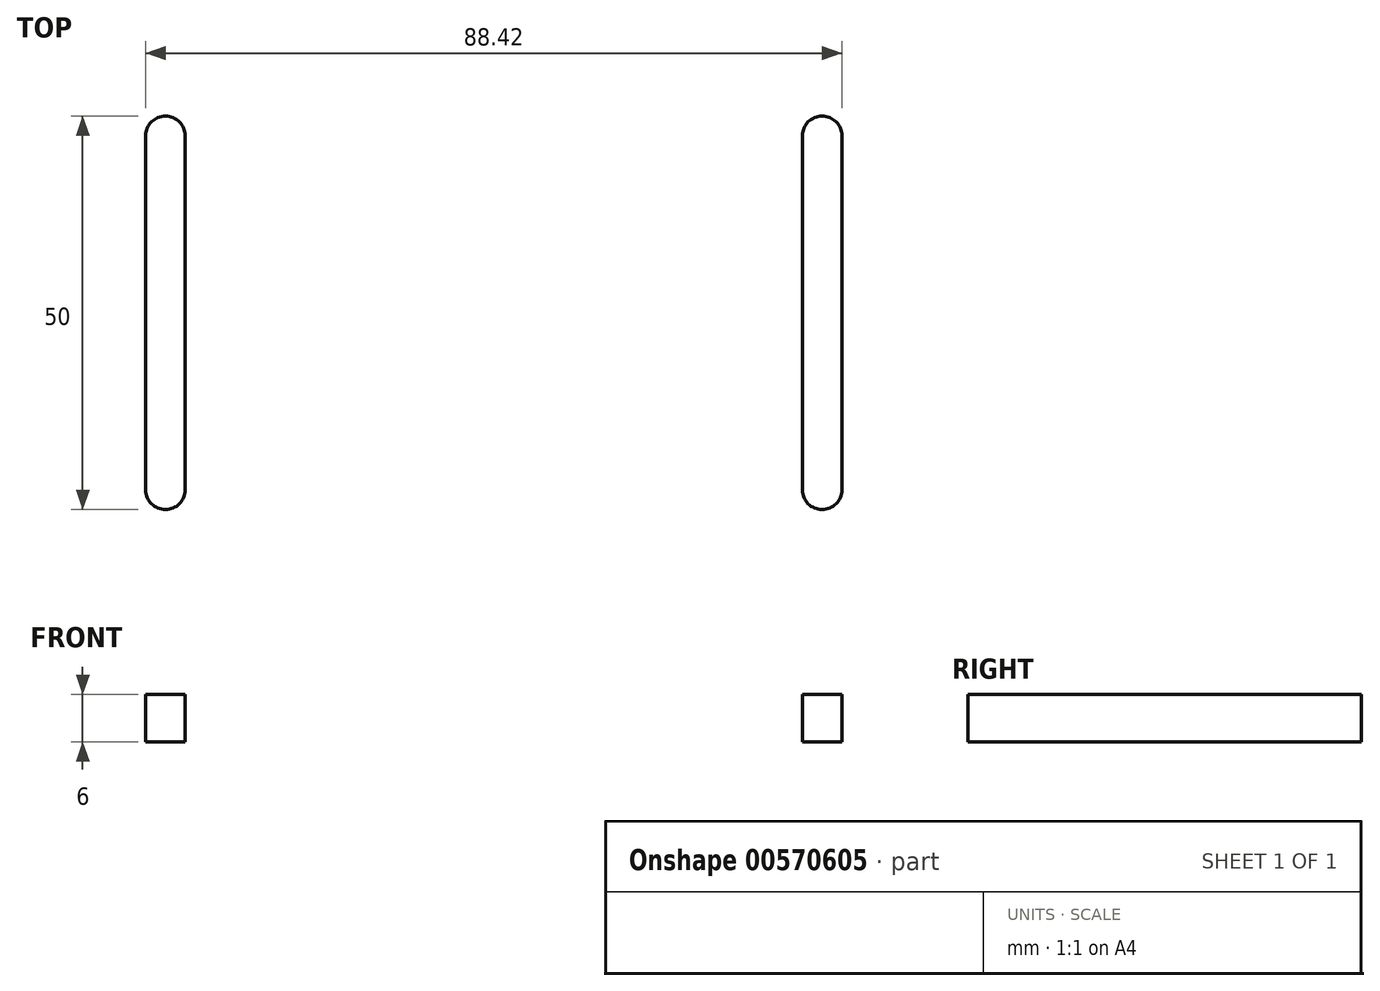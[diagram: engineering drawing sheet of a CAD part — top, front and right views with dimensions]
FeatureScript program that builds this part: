
annotation { "Feature Type Name" : "Feature", "Feature Type Description" : "" }
export const myFeature = defineFeature(function(context is Context, id is Id, definition is map)
    precondition{}
    {
        {
            var Q0;
            Q0=qCreatedBy(makeId("Top.planeOp"),FACE);
            var sketch = newSketch(context, id + "F0", { "sketchPlane" : qUnion([Q0])});
            skLineSegment(sketch, "E0.bottom", {"start": v(0, 0) * mm, "end": v(50, 0) * mm});
            skLineSegment(sketch, "E0.top", {"start": v(0, 70) * mm, "end": v(50, 70) * mm});
            skLineSegment(sketch, "E0.left", {"start": v(0, 0) * mm, "end": v(0, 70) * mm});
            skLineSegment(sketch, "E0.right", {"start": v(50, 0) * mm, "end": v(50, 70) * mm});
            skSolve(sketch);
        }
        {
            var Q0;
            Q0=makeQuery(id+"F0.imprint","IMPRINT",FACE,{"disambiguationData":[TD([[makeQuery(id+"F0.imprint","IMPRINT",EDGE,{"derivedFrom":sQuery(id+"F0.wireOp",EDGE,"E0.bottom")}),1.0]])]});
            extrude(context, id + "F1", {"entities" : qUnion([Q0]), "depth" : 3 * mm, "offsetDistance" : 25 * mm});
        }
        {
            var Q0;
            Q0=makeQuery(id+"F1.opExtrude","CAP_FACE",FACE,{"disambiguationData":[OSD([sQuery(id+"F0.wireOp",EDGE,"E0.bottom"),sQuery(id+"F0.wireOp",EDGE,"E0.top"),sQuery(id+"F0.wireOp",EDGE,"E0.left"),sQuery(id+"F0.wireOp",EDGE,"E0.right")])],"isStart":false});
            var sketch = newSketch(context, id + "F2", { "sketchPlane" : qUnion([Q0])});
            skLineSegment(sketch, "E1", {"start": v(35, 20) * mm, "end": v(35, 60) * mm});
            skSolve(sketch);
        }
        {
            var Q0;
            Q0=sQuery(id+"F2.wireOp",VERTEX,"E1.start");
            var Q1;
            Q1=sQuery(id+"F2.wireOp",VERTEX,"E1.end");
            var Q2;
            Q2=makeQuery(id+"F1.opExtrude","SWEPT_BODY",BODY,{"disambiguationData":[OSD([sQuery(id+"F0.wireOp",EDGE,"E0.bottom"),sQuery(id+"F0.wireOp",EDGE,"E0.top"),sQuery(id+"F0.wireOp",EDGE,"E0.left"),sQuery(id+"F0.wireOp",EDGE,"E0.right")])]});
            hole(context, id + "F3", {"style" : HoleStyle.SIMPLE, "endStyle" : HoleEndStyle.THROUGH, "holeDiameter" : 3 * mm, "isTappedThrough" : true, "tappedDepth" : 12 * mm, "tapClearance" : 3, "locations" : qUnion([Q0, Q1]), "scope" : qUnion([Q2])});
        }
        {
            var Q0;
            Q0=makeQuery(id+"F1.opExtrude","CAP_FACE",FACE,{"disambiguationData":[OSD([sQuery(id+"F0.wireOp",EDGE,"E0.bottom"),sQuery(id+"F0.wireOp",EDGE,"E0.top"),sQuery(id+"F0.wireOp",EDGE,"E0.left"),sQuery(id+"F0.wireOp",EDGE,"E0.right")])],"isStart":false});
            var sketch = newSketch(context, id + "F4", { "sketchPlane" : qUnion([Q0])});
            skLineSegment(sketch, "E2", {"start": v(41.71, 59.96) * mm, "end": v(41.71, 14.96) * mm});
            skSolve(sketch);
        }
        {
            var Q0;
            Q0=makeQuery(id+"F4.imprint","IMPRINT",FACE,{"disambiguationData":[TD([[makeQuery(id+"F4.imprint","IMPRINT",EDGE,{"derivedFrom":makeQuery(id+"F1.opExtrude","CAP_EDGE",EDGE,{"disambiguationData":[OSD([sQuery(id+"F0.wireOp",EDGE,"E0.bottom")])],"isStart":false})}),1.0]])]});
            var sketch = newSketch(context, id + "F5", { "sketchPlane" : qUnion([Q0])});
            skLineSegment(sketch, "E3.JUB.JUB", {"start": v(41.71, 59.96) * mm, "end": v(41.71, 14.96) * mm, "construction": true});
            skArc(sketch, "E3.0.startCap", {"start": v(39.21, 59.96) * mm, "mid": v(41.71, 62.46) * mm, "end": v(44.21, 59.96) * mm});
            skArc(sketch, "E3.0.endCap", {"start": v(44.21, 14.96) * mm, "mid": v(41.71, 12.46) * mm, "end": v(39.21, 14.96) * mm});
            skLineSegment(sketch, "E3.0.left", {"start": v(44.21, 59.96) * mm, "end": v(44.21, 14.96) * mm});
            skLineSegment(sketch, "E3.0.right", {"start": v(39.21, 59.96) * mm, "end": v(39.21, 14.96) * mm});
            skSolve(sketch);
        }
        {
            var Q0;
            Q0=makeQuery(id+"F5.imprint","IMPRINT",FACE,{"disambiguationData":[TD([[makeQuery(id+"F5.imprint","IMPRINT",EDGE,{"derivedFrom":sQuery(id+"F5.wireOp",EDGE,"E3.0.startCap")}),-1.0]])]});
            extrude(context, id + "F6", {"entities" : qUnion([Q0]), "operationType" : NewBodyOperationType.REMOVE, "depth" : -33 * mm, "offsetDistance" : 25 * mm});
        }
        {
            var Q0;
            Q0=makeQuery(id+"F1.opExtrude","SWEPT_BODY",BODY,{"disambiguationData":[OSD([sQuery(id+"F0.wireOp",EDGE,"E0.bottom"),sQuery(id+"F0.wireOp",EDGE,"E0.top"),sQuery(id+"F0.wireOp",EDGE,"E0.left"),sQuery(id+"F0.wireOp",EDGE,"E0.right")])]});
            var Q1;
            Q1=qCreatedBy(makeId("Top.planeOp"),FACE);
            mirror(context, id + "F7", {"operationType" : NewBodyOperationType.ADD, "entities" : qUnion([Q0]), "mirrorPlane" : qUnion([Q1])});
        }
        {
            var Q0;
            Q0=makeQuery(id+"F1.opExtrude","SWEPT_BODY",BODY,{"disambiguationData":[OSD([sQuery(id+"F0.wireOp",EDGE,"E0.bottom"),sQuery(id+"F0.wireOp",EDGE,"E0.top"),sQuery(id+"F0.wireOp",EDGE,"E0.left"),sQuery(id+"F0.wireOp",EDGE,"E0.right")])]});
            var Q1;
            Q1=qCreatedBy(makeId("Right.planeOp"),FACE);
            mirror(context, id + "F8", {"operationType" : NewBodyOperationType.ADD, "entities" : qUnion([Q0]), "mirrorPlane" : qUnion([Q1])});
        }
    });
